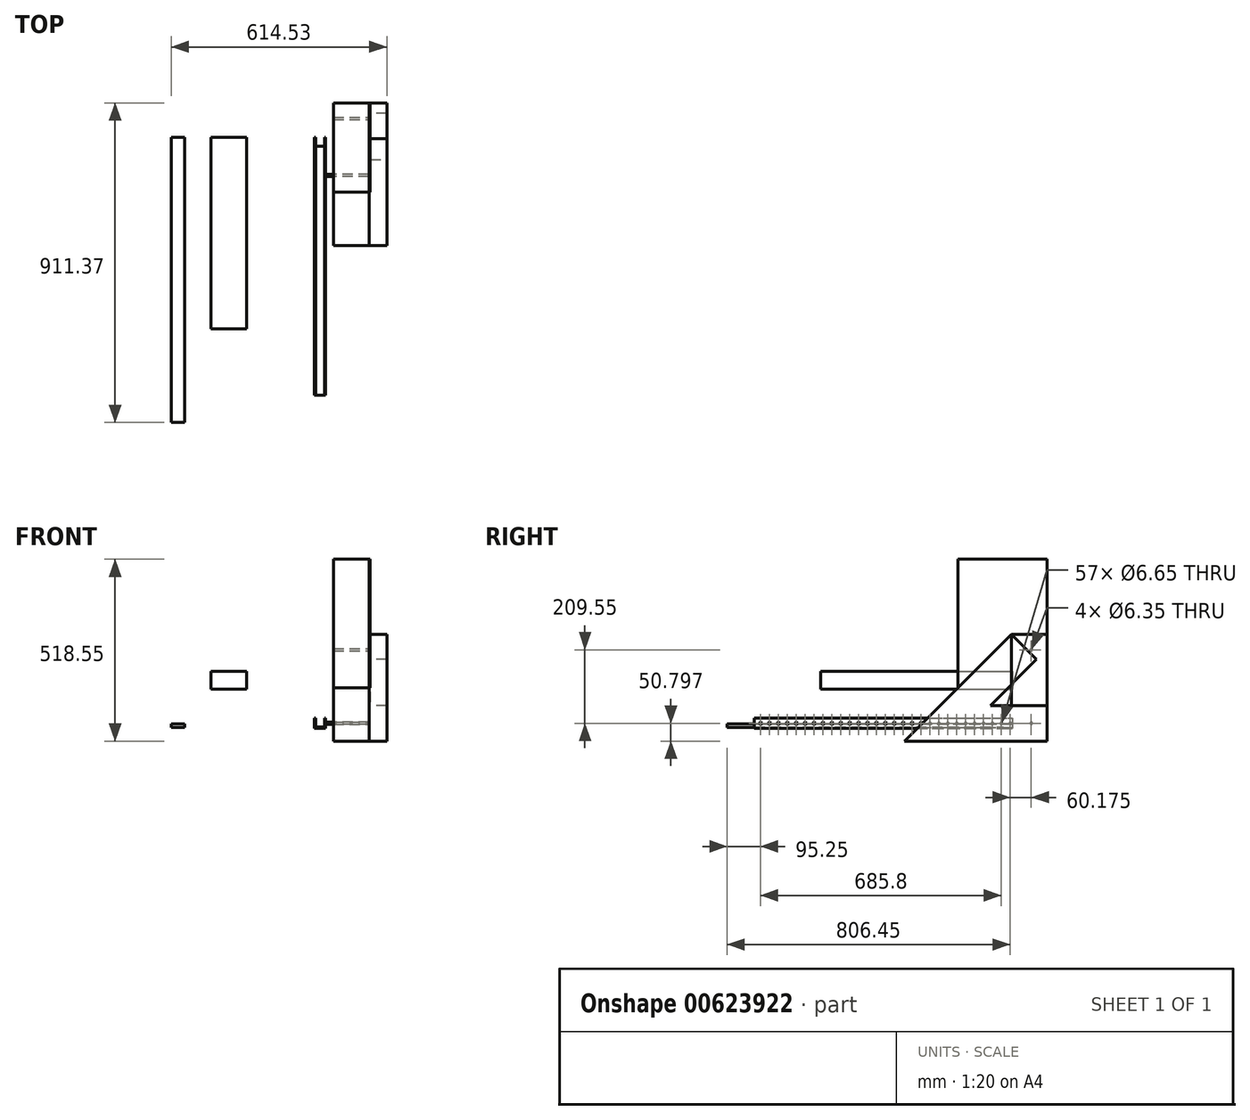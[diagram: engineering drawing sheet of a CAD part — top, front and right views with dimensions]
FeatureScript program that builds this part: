
annotation { "Feature Type Name" : "Feature", "Feature Type Description" : "" }
export const myFeature = defineFeature(function(context is Context, id is Id, definition is map)
    precondition{}
    {
        {
            var Q0;
            Q0=qCreatedBy(makeId("Front.planeOp"),FACE);
            var sketch = newSketch(context, id + "F0", { "sketchPlane" : qUnion([Q0])});
            skLineSegment(sketch, "E0", {"start": v(-56.5, 60.32) * mm, "end": v(-56.5, 31.75) * mm});
            skLineSegment(sketch, "E1", {"start": v(-56.5, 31.75) * mm, "end": v(-24.75, 31.75) * mm});
            skLineSegment(sketch, "E2", {"start": v(-24.75, 31.75) * mm, "end": v(-24.75, 60.33) * mm});
            skLineSegment(sketch, "E3", {"start": v(-24.75, 60.33) * mm, "end": v(-27.93, 60.33) * mm});
            skLineSegment(sketch, "E4", {"start": v(-27.93, 60.33) * mm, "end": v(-27.93, 34.92) * mm});
            skLineSegment(sketch, "E5", {"start": v(-27.93, 34.92) * mm, "end": v(-53.33, 34.92) * mm});
            skLineSegment(sketch, "E6", {"start": v(-53.33, 34.92) * mm, "end": v(-53.33, 60.32) * mm});
            skLineSegment(sketch, "E7", {"start": v(-53.33, 60.32) * mm, "end": v(-56.5, 60.32) * mm});
            skSolve(sketch);
        }
        {
            var Q0;
            Q0=qSketchRegion(id+"F0",true);
            extrude(context, id + "F1", {"entities" : qUnion([Q0]), "depth" : 735 * mm});
        }
        {
            var Q0;
            Q0=makeQuery(id+"F1.opExtrude","SWEPT_FACE",FACE,{"disambiguationData":[OSD([sQuery(id+"F0.wireOp",EDGE,"E2")])]});
            var sketch = newSketch(context, id + "F2", { "sketchPlane" : qUnion([Q0])});
            skLineSegment(sketch, "E8", {"start": v(-735.01, 46.04) * mm, "end": v(0, 46.04) * mm, "construction": true});
            skCircle(sketch, "E9", {"center": v(-6.35, 46.04) * mm, "radius": 3.18 * mm});
            skCircle(sketch, "E10", {"center": v(-31.75, 46.04) * mm, "radius": 3.32 * mm});
            skCircle(sketch, "E11.1.0.0", {"center": v(-57.15, 46.04) * mm, "radius": 3.32 * mm});
            skCircle(sketch, "E11.2.0.0", {"center": v(-82.55, 46.04) * mm, "radius": 3.32 * mm});
            skCircle(sketch, "E11.3.0.0", {"center": v(-107.95, 46.04) * mm, "radius": 3.32 * mm});
            skCircle(sketch, "E11.4.0.0", {"center": v(-133.35, 46.04) * mm, "radius": 3.32 * mm});
            skCircle(sketch, "E11.5.0.0", {"center": v(-158.75, 46.04) * mm, "radius": 3.32 * mm});
            skCircle(sketch, "E11.6.0.0", {"center": v(-184.15, 46.04) * mm, "radius": 3.32 * mm});
            skCircle(sketch, "E11.7.0.0", {"center": v(-209.55, 46.04) * mm, "radius": 3.32 * mm});
            skCircle(sketch, "E11.8.0.0", {"center": v(-234.95, 46.04) * mm, "radius": 3.32 * mm});
            skCircle(sketch, "E11.9.0.0", {"center": v(-260.35, 46.04) * mm, "radius": 3.32 * mm});
            skCircle(sketch, "E11.10.0.0", {"center": v(-285.75, 46.04) * mm, "radius": 3.32 * mm});
            skCircle(sketch, "E11.11.0.0", {"center": v(-311.15, 46.04) * mm, "radius": 3.32 * mm});
            skCircle(sketch, "E11.12.0.0", {"center": v(-336.55, 46.04) * mm, "radius": 3.32 * mm});
            skCircle(sketch, "E11.13.0.0", {"center": v(-361.95, 46.04) * mm, "radius": 3.32 * mm});
            skCircle(sketch, "E11.14.0.0", {"center": v(-387.35, 46.04) * mm, "radius": 3.32 * mm});
            skCircle(sketch, "E11.15.0.0", {"center": v(-412.75, 46.04) * mm, "radius": 3.32 * mm});
            skCircle(sketch, "E11.16.0.0", {"center": v(-438.15, 46.04) * mm, "radius": 3.32 * mm});
            skCircle(sketch, "E11.17.0.0", {"center": v(-463.55, 46.04) * mm, "radius": 3.32 * mm});
            skCircle(sketch, "E11.18.0.0", {"center": v(-488.95, 46.04) * mm, "radius": 3.32 * mm});
            skCircle(sketch, "E11.19.0.0", {"center": v(-514.35, 46.04) * mm, "radius": 3.32 * mm});
            skCircle(sketch, "E11.20.0.0", {"center": v(-539.75, 46.04) * mm, "radius": 3.32 * mm});
            skCircle(sketch, "E11.21.0.0", {"center": v(-565.15, 46.04) * mm, "radius": 3.32 * mm});
            skCircle(sketch, "E11.22.0.0", {"center": v(-590.55, 46.04) * mm, "radius": 3.32 * mm});
            skCircle(sketch, "E11.23.0.0", {"center": v(-615.95, 46.04) * mm, "radius": 3.32 * mm});
            skCircle(sketch, "E11.24.0.0", {"center": v(-641.35, 46.04) * mm, "radius": 3.32 * mm});
            skCircle(sketch, "E11.25.0.0", {"center": v(-666.75, 46.04) * mm, "radius": 3.32 * mm});
            skCircle(sketch, "E11.26.0.0", {"center": v(-692.15, 46.04) * mm, "radius": 3.32 * mm});
            skCircle(sketch, "E11.27.0.0", {"center": v(-717.55, 46.04) * mm, "radius": 3.32 * mm});
            skCircle(sketch, "E11.28.0.0", {"center": v(-742.95, 46.04) * mm, "radius": 3.32 * mm});
            skLineSegment(sketch, "E11.direction1", {"start": v(-31.75, 46.04) * mm, "end": v(-57.15, 46.04) * mm, "construction": true});
            skSolve(sketch);
        }
        {
            var Q0;
            Q0=qSketchRegion(id+"F2",true);
            var Q1;
            Q1=makeQuery(id+"F1.opExtrude","SWEPT_FACE",FACE,{"disambiguationData":[OSD([sQuery(id+"F0.wireOp",EDGE,"E0")])]});
            extrude(context, id + "F3", {"entities" : qUnion([Q0]), "operationType" : NewBodyOperationType.REMOVE, "endBound" : BoundingType.UP_TO_SURFACE, "oppositeDirection" : true, "endBoundEntityFace" : qUnion([Q1]), "depth" : 25.4 * mm});
        }
        {
            var Q0;
            Q0=makeQuery(id+"F1.opExtrude","SWEPT_FACE",FACE,{"disambiguationData":[OSD([sQuery(id+"F0.wireOp",EDGE,"E4")])]});
            var sketch = newSketch(context, id + "F4", { "sketchPlane" : qUnion([Q0])});
            skCircle(sketch, "E12.0", {"center": v(107.95, 46.04) * mm, "radius": 3.32 * mm});
            skSolve(sketch);
        }
        {
            var Q0;
            Q0=qSketchRegion(id+"F4",true);
            extrude(context, id + "F5", {"entities" : qUnion([Q0]), "oppositeDirection" : true, "depth" : 127 * mm});
        }
        {
            var Q0;
            Q0=makeQuery(id+"F5.opExtrude","CAP_FACE",FACE,{"disambiguationData":[OSD([sQuery(id+"F4.wireOp",EDGE,"E12.0")])],"isStart":false});
            var sketch = newSketch(context, id + "F6", { "sketchPlane" : qUnion([Q0])});
            skLineSegment(sketch, "E13.bottom", {"start": v(98.57, 0) * mm, "end": v(-155.43, 0) * mm});
            skLineSegment(sketch, "E13.top", {"start": v(98.57, 513.79) * mm, "end": v(-155.43, 513.79) * mm});
            skLineSegment(sketch, "E13.left", {"start": v(98.57, 0) * mm, "end": v(98.57, 513.79) * mm});
            skLineSegment(sketch, "E13.right", {"start": v(-155.43, 0) * mm, "end": v(-155.43, 513.79) * mm});
            skSolve(sketch);
        }
        {
            var Q0;
            Q0=qSketchRegion(id+"F6",true);
            extrude(context, id + "F7", {"entities" : qUnion([Q0]), "operationType" : NewBodyOperationType.ADD, "depth" : 3.17 * mm});
        }
        {
            var Q0;
            Q0=makeQuery(id+"F1.opExtrude","SWEPT_FACE",FACE,{"disambiguationData":[OSD([sQuery(id+"F0.wireOp",EDGE,"E1")])]});
            var sketch = newSketch(context, id + "F8", { "sketchPlane" : qUnion([Q0])});
            skLineSegment(sketch, "E14.0", {"start": v(-53.33, 735.01) * mm, "end": v(-53.33, 0) * mm});
            skLineSegment(sketch, "E15.0", {"start": v(-27.93, 735.01) * mm, "end": v(-27.93, 0) * mm});
            skLineSegment(sketch, "E16", {"start": v(-53.33, 0) * mm, "end": v(-27.93, 0) * mm});
            skLineSegment(sketch, "E17", {"start": v(-53.33, 25.4) * mm, "end": v(-27.93, 25.4) * mm});
            skSolve(sketch);
        }
        {
            var Q0;
            Q0=qSketchRegion(id+"F8",true);
            extrude(context, id + "F9", {"entities" : qUnion([Q0]), "operationType" : NewBodyOperationType.REMOVE, "oppositeDirection" : true, "depth" : 25.4 * mm});
        }
        {
            var Q0;
            Q0=makeQuery(id+"F7.opExtrude","CAP_FACE",FACE,{"disambiguationData":[OSD([sQuery(id+"F6.wireOp",EDGE,"E13.bottom"),sQuery(id+"F6.wireOp",EDGE,"E13.top"),sQuery(id+"F6.wireOp",EDGE,"E13.left"),sQuery(id+"F6.wireOp",EDGE,"E13.right")])],"isStart":true});
            var sketch = newSketch(context, id + "F10", { "sketchPlane" : qUnion([Q0])});
            skLineSegment(sketch, "E18", {"start": v(107.95, 46.04) * mm, "end": v(-98.57, 46.04) * mm, "construction": true});
            skLineSegment(sketch, "E19", {"start": v(-98.57, -4.76) * mm, "end": v(155.43, -4.76) * mm});
            skLineSegment(sketch, "E20", {"start": v(155.43, -4.76) * mm, "end": v(155.43, 96.84) * mm});
            skLineSegment(sketch, "E21", {"start": v(155.43, 96.84) * mm, "end": v(-98.57, 96.84) * mm});
            skLineSegment(sketch, "E22", {"start": v(-98.57, 96.84) * mm, "end": v(-98.57, -4.76) * mm});
            skSolve(sketch);
        }
        {
            var Q0;
            Q0=qSketchRegion(id+"F10",true);
            extrude(context, id + "F11", {"entities" : qUnion([Q0]), "oppositeDirection" : true, "depth" : 50.8 * mm});
        }
        {
            var Q0;
            Q0=makeQuery(id+"F11.opExtrude","SWEPT_FACE",FACE,{"disambiguationData":[OSD([sQuery(id+"F10.wireOp",EDGE,"E21")])]});
            var sketch = newSketch(context, id + "F12", { "sketchPlane" : qUnion([Q0])});
            skLineSegment(sketch, "E23.0.0", {"start": v(99.07, 98.57) * mm, "end": v(99.07, -155.43) * mm});
            skLineSegment(sketch, "E23.0.1", {"start": v(99.07, -155.43) * mm, "end": v(149.87, -155.43) * mm});
            skLineSegment(sketch, "E23.0.2", {"start": v(149.87, -155.43) * mm, "end": v(149.87, 98.57) * mm});
            skLineSegment(sketch, "E23.0.3", {"start": v(149.87, 98.57) * mm, "end": v(99.07, 98.57) * mm});
            skLineSegment(sketch, "E24", {"start": v(149.87, -3.03) * mm, "end": v(99.07, -3.03) * mm});
            skSolve(sketch);
        }
        {
            var Q0;
            {var subQ0=sQuery(id+"F12.wireOp",EDGE,"E23.0.3");Q0=makeQuery(id+"F12.imprint","IMPRINT",FACE,{"disambiguationData":[TD([[makeQuery(id+"F12.imprint","IMPRINT",EDGE,{"derivedFrom":subQ0}),1.0]])]});}
            extrude(context, id + "F13", {"entities" : qUnion([Q0]), "depth" : 203.2 * mm});
        }
        {
            var Q0;
            Q0=makeQuery(id+"F7.opExtrude","CAP_FACE",FACE,{"disambiguationData":[OSD([sQuery(id+"F6.wireOp",EDGE,"E13.bottom"),sQuery(id+"F6.wireOp",EDGE,"E13.top"),sQuery(id+"F6.wireOp",EDGE,"E13.left"),sQuery(id+"F6.wireOp",EDGE,"E13.right")])],"isStart":true});
            var sketch = newSketch(context, id + "F14", { "sketchPlane" : qUnion([Q0])});
            skCircle(sketch, "E25.0", {"center": v(-53.83, 46.04) * mm, "radius": 3.18 * mm});
            skLineSegment(sketch, "E26", {"start": v(-53.83, 46.04) * mm, "end": v(-53.83, 255.59) * mm, "construction": true});
            skCircle(sketch, "E27", {"center": v(-53.83, 255.59) * mm, "radius": 3.18 * mm});
            skSolve(sketch);
        }
        {
            var Q0;
            Q0=makeQuery(id+"F13.opExtrude","SWEPT_BODY",BODY,{"disambiguationData":[OSD([sQuery(id+"F12.wireOp",EDGE,"E23.0.0"),sQuery(id+"F12.wireOp",EDGE,"E23.0.2"),sQuery(id+"F12.wireOp",EDGE,"E23.0.3"),sQuery(id+"F12.wireOp",EDGE,"E24")])]});
            var Q1;
            Q1=makeQuery(id+"F13.opExtrude","CAP_EDGE",EDGE,{"disambiguationData":[OSD([sQuery(id+"F12.wireOp",EDGE,"E24")])],"isStart":false});
            transform(context, id + "F15", {"entities" : qUnion([Q0]), "transformType" : TransformType.ROTATION, "transformAxis" : qUnion([Q1]), "angle" : 45 * degree, "makeCopy" : true});
        }
        {
            var Q0;
            Q0=makeQuery(id+"F15.opPattern","COPY",FACE,{"derivedFrom":makeQuery(id+"F13.opExtrude","CAP_FACE",FACE,{"disambiguationData":[OSD([sQuery(id+"F12.wireOp",EDGE,"E23.0.0"),sQuery(id+"F12.wireOp",EDGE,"E23.0.2"),sQuery(id+"F12.wireOp",EDGE,"E23.0.3"),sQuery(id+"F12.wireOp",EDGE,"E24")])],"isStart":true}),"instanceName":"1"});
            var Q1;
            Q1=makeQuery(id+"F11.opExtrude","SWEPT_FACE",FACE,{"disambiguationData":[OSD([sQuery(id+"F10.wireOp",EDGE,"E21")])]});
            extrude(context, id + "F16", {"entities" : qUnion([Q0]), "operationType" : NewBodyOperationType.ADD, "endBound" : BoundingType.UP_TO_SURFACE, "endBoundEntityFace" : qUnion([Q1]), "depth" : 25.4 * mm});
        }
        {
            var Q0;
            Q0=makeQuery(id+"F11.opExtrude","SWEPT_FACE",FACE,{"disambiguationData":[OSD([sQuery(id+"F10.wireOp",EDGE,"E20")])]});
            var sketch = newSketch(context, id + "F17", { "sketchPlane" : qUnion([Q0])});
            skLineSegment(sketch, "E28.0.0", {"start": v(99.07, 96.84) * mm, "end": v(99.07, -4.76) * mm});
            skLineSegment(sketch, "E28.0.1", {"start": v(99.07, -4.76) * mm, "end": v(149.87, -4.76) * mm});
            skLineSegment(sketch, "E28.0.2", {"start": v(149.87, -4.76) * mm, "end": v(149.87, 96.84) * mm});
            skLineSegment(sketch, "E28.0.3", {"start": v(149.87, 96.84) * mm, "end": v(99.07, 96.84) * mm});
            skSolve(sketch);
        }
        {
            var Q0;
            Q0=qSketchRegion(id+"F17",true);
            var Q1;
            {var subQ0=sQuery(id+"F12.wireOp",EDGE,"E24");Q1=makeQuery(id+"F16.boolean.opBoolean","MERGE",FACE,{"derivedFrom":[makeQuery(id+"F15.opPattern","COPY",FACE,{"derivedFrom":makeQuery(id+"F13.opExtrude","SWEPT_FACE",FACE,{"disambiguationData":[OSD([subQ0])]}),"instanceName":"1"}),makeQuery(id+"F16.opExtrude","SWEPT_FACE",FACE,{"disambiguationData":[OSD([subQ0])]})]});}
            extrude(context, id + "F18", {"entities" : qUnion([Q0]), "operationType" : NewBodyOperationType.ADD, "endBound" : BoundingType.UP_TO_SURFACE, "endBoundEntityFace" : qUnion([Q1]), "depth" : 25.4 * mm});
        }
        {
            var Q0;
            Q0=makeQuery(id+"F18.boolean.opBoolean","MERGE",FACE,{"derivedFrom":[makeQuery(id+"F11.opExtrude","CAP_FACE",FACE,{"disambiguationData":[OSD([sQuery(id+"F10.wireOp",EDGE,"E19"),sQuery(id+"F10.wireOp",EDGE,"E20"),sQuery(id+"F10.wireOp",EDGE,"E21"),sQuery(id+"F10.wireOp",EDGE,"E22")])],"isStart":true}),makeQuery(id+"F18.opExtrude","SWEPT_FACE",FACE,{"disambiguationData":[OSD([sQuery(id+"F17.wireOp",EDGE,"E28.0.0")])]})]});
            var sketch = newSketch(context, id + "F19", { "sketchPlane" : qUnion([Q0])});
            skCircle(sketch, "E29.0", {"center": v(107.95, 46.04) * mm, "radius": 3.32 * mm});
            skCircle(sketch, "E30.0", {"center": v(-53.83, 46.04) * mm, "radius": 3.18 * mm});
            skCircle(sketch, "E31.0", {"center": v(-53.83, 255.59) * mm, "radius": 3.18 * mm});
            skSolve(sketch);
        }
        {
            var Q0;
            Q0=makeQuery(id+"F14.imprint","IMPRINT",FACE,{"disambiguationData":[TD([[makeQuery(id+"F14.imprint","IMPRINT",EDGE,{"derivedFrom":sQuery(id+"F14.wireOp",EDGE,"E27")}),1.0]])]});
            extrude(context, id + "F20", {"entities" : qUnion([Q0]), "depth" : 101.6 * mm});
        }
        {
            var Q0;
            Q0=makeQuery(id+"F19.imprint","IMPRINT",FACE,{"disambiguationData":[TD([[makeQuery(id+"F19.imprint","IMPRINT",EDGE,{"derivedFrom":sQuery(id+"F19.wireOp",EDGE,"E29.0")}),1.0]])]});
            extrude(context, id + "F21", {"entities" : qUnion([Q0]), "depth" : 101.6 * mm});
        }
        {
            var Q0;
            Q0=qCreatedBy(makeId("Front.planeOp"),FACE);
            var sketch = newSketch(context, id + "F22", { "sketchPlane" : qUnion([Q0])});
            skLineSegment(sketch, "E32.bottom", {"start": v(-464.66, 44.76) * mm, "end": v(-426.56, 44.76) * mm});
            skLineSegment(sketch, "E32.top", {"start": v(-464.66, 34.72) * mm, "end": v(-426.56, 34.72) * mm});
            skLineSegment(sketch, "E32.left", {"start": v(-464.66, 44.76) * mm, "end": v(-464.66, 34.72) * mm});
            skLineSegment(sketch, "E32.right", {"start": v(-426.56, 44.76) * mm, "end": v(-426.56, 34.72) * mm});
            skSolve(sketch);
        }
        {
            var Q0;
            Q0=qSketchRegion(id+"F22",true);
            extrude(context, id + "F23", {"entities" : qUnion([Q0]), "depth" : 812.8 * mm});
        }
        {
            var Q0;
            Q0=qCreatedBy(makeId("Front.planeOp"),FACE);
            var sketch = newSketch(context, id + "F24", { "sketchPlane" : qUnion([Q0])});
            skLineSegment(sketch, "E33.bottom", {"start": v(-351.89, 193.68) * mm, "end": v(-250.29, 193.68) * mm});
            skLineSegment(sketch, "E33.top", {"start": v(-351.89, 142.88) * mm, "end": v(-250.29, 142.88) * mm});
            skLineSegment(sketch, "E33.left", {"start": v(-351.89, 193.68) * mm, "end": v(-351.89, 142.88) * mm});
            skLineSegment(sketch, "E33.right", {"start": v(-250.29, 193.68) * mm, "end": v(-250.29, 142.88) * mm});
            skSolve(sketch);
        }
        {
            var Q0;
            Q0=qSketchRegion(id+"F24",true);
            extrude(context, id + "F25", {"entities" : qUnion([Q0]), "depth" : 546.1 * mm});
        }
    });
